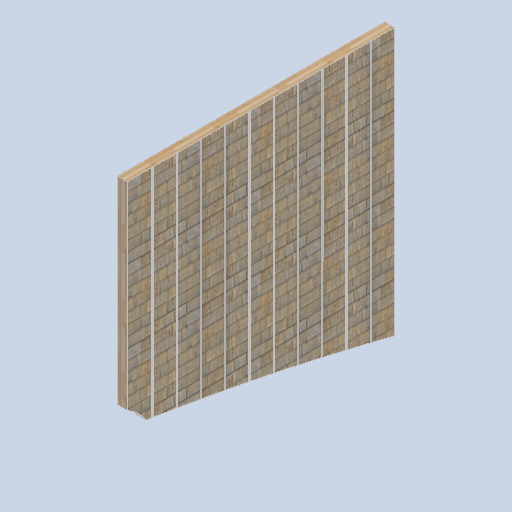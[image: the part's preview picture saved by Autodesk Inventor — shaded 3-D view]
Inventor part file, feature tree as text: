
AUTODESK INVENTOR PART (.ipt)
format: ipt  version: 2024.2 (Build 282272000, 272)  size: 331,264 bytes
history: native  units: in
note: dims shown in document units (in); Inventor stores cm internally (conversion verified against a paired STEP export)
features: other x3, sketch x2
ambient origin geometry x8: Origin, YZ Plane, XZ Plane, XY Plane, X Axis, Y Axis, Z Axis, Center Point
bodies: Solid1 (feature_tree)
feature tree (5):
  other  "side_wall_01_MIR.ipt"
  other  "Solid1::side_wall_01_MIR.ipt"
  other  "TaggingFeature1"
  sketch  "Sketch1"  dims[d0=0.3937in]
  sketch  "Sketch2"
